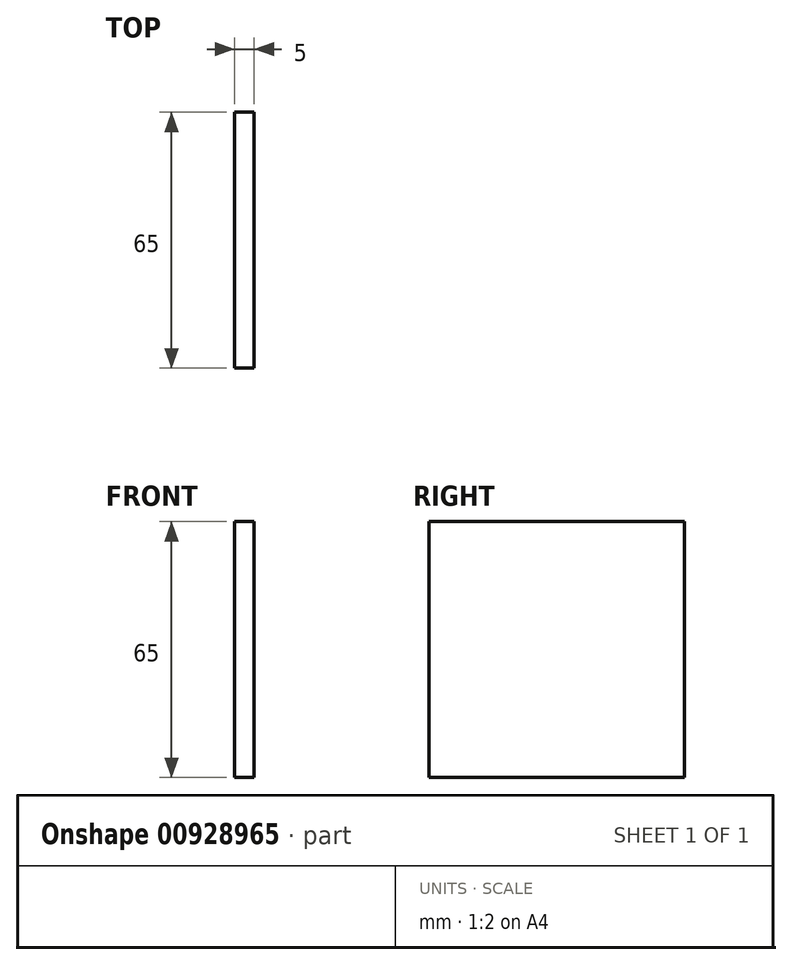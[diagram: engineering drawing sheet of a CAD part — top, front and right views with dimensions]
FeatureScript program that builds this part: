
annotation { "Feature Type Name" : "Feature", "Feature Type Description" : "" }
export const myFeature = defineFeature(function(context is Context, id is Id, definition is map)
    precondition{}
    {
        {
            var Q0;
            Q0=qCreatedBy(makeId("Right.planeOp"),FACE);
            var sketch = newSketch(context, id + "F0", { "sketchPlane" : qUnion([Q0])});
            skLineSegment(sketch, "E0.bottom", {"start": v(32.5, -32.5) * mm, "end": v(-32.5, -32.5) * mm});
            skLineSegment(sketch, "E0.top", {"start": v(32.5, 32.5) * mm, "end": v(-32.5, 32.5) * mm});
            skLineSegment(sketch, "E0.left", {"start": v(32.5, -32.5) * mm, "end": v(32.5, 32.5) * mm});
            skLineSegment(sketch, "E0.right", {"start": v(-32.5, -32.5) * mm, "end": v(-32.5, 32.5) * mm});
            skPoint(sketch, "E0.middle", {"position": v(0, 0) * mm});
            skSolve(sketch);
        }
        {
            var Q0;
            Q0 = qSketchRegion(id + "F0", true);
            extrude(context, id + "F1", {"entities" : qUnion([Q0]), "depth" : 5 * mm, "offsetDistance" : 25.4 * mm});
        }
    });
